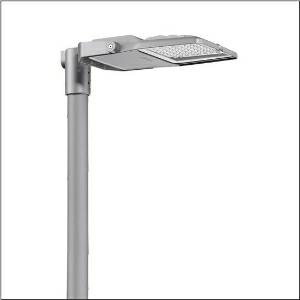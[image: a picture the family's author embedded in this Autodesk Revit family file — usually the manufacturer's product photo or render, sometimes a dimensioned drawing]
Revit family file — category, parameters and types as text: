
# Revit family: floodlight_fl_21_mini___pl43_5xa7775d2a3a_0001
name_source: partatom
category: Lighting Fixtures
units: mm (PartAtom-declared; Revit-internal decimal feet)

## family parameters
Cut with Voids When Loaded = No
Host = Face
Light Source = No
Part Type = Normal
Room Calculation Point = No
Round Connector Dimension = Use Diameter
Shared = No

## types (1)
- --- (1 x LED, 18300 lm, 142.9 W, 3000K)
    Apparent Load = 143 VA
    CIE Flux Codes = 27 78 99 100 100
    Color Rendering = 70
    Color Temperature = 3000K
    Default Elevation = 1800 mm
    Description = Floodlight FL 21 mini, floodlight, primary light control with lens, of PMMA, primary optical cover: protective disc, of toughened safety glass, transparent, light distribution: PL43, light emission: direct distribution, installation type: surface-mounted, LED, High Power LED, rated luminous flux: 18.300lm, luminous efficacy: 128lm/W, light colour: 730, colour temperature: 3000K, control gear: Smart Interface (Zhaga), control: flexible luminous flux parameterisation, time-dependent luminous flux control, constant luminous flux control, overheat protection, pre-setting: logarithmic dimming characteristic, with terminal, 6-pole, mains connection: 220..240V, AC, 50/60Hz, start of lifetime: 143W, end of service life: 151W, reduction: 63W, luminaire housing, of diecast aluminium, powder-coated, Siteco® metallic grey (DB 702S), corrosivity category C5 mid according to DIN EN ISO 12944, suitable for swimming pools, chlorine-resistant, sealing non-destructively replaceable, please order mast flange separately, mast bracket, of steel, galvanised, powder-coated, Siteco® metallic grey (DB 702S), Smart Interface above, protection rating (complete): IP66, insulation class (complete): insulation class II (safety insulation), certification: CE, ENEC, VDE, protection symbol: D, impact resistance: IK08, permissible operating ambient temperature: -40..+40°C, permissible operating ambient temperature for outdoor applications: -40..+50°C, standard: DIN EN 12944, LABS conformity tested according to VDMA 24364:2018-05, packaging unit: 1 piece

Light Distribution: PL43
    Height = 70 mm
    Lamp = 1 x LED
    Lamp Light Flux = 18300 lm
    Lamp Power = 142.9 W
    Lamp count = 1
    Length = 485 mm
    Luminous efficacy = 128 lm/W
    Manufacturer = Siteco
    ModVariant = No
    Model = 5XA7775D2A3A
    Number of Poles = 1
    OnlyDefault = Yes
    Power Factor = 1
    Product Name = Floodlight FL 21 mini | PL43
    Product group = floodlight | pylon annexe
    ProductGroupID = 6200
    Protection Class = Protection class II
    Protection Degree = IP 66
    RLX_Detail_Level = 1
    RLX_Emergency_Light_Flux = 0 lm
    RLX_Emergency_Type = 0
    RLX_Emergency_Type_DB = No
    RlxData = <blob elided: 101321 chars, md5=4b30785b>
    Socket = socket
    Standby Power = 0 W
    System Light Flux = 18300 lm
    System Power = 143 W
    Type Comments = factory setting: luminous flux: 100 % | dim-lin: 254 | 730 mA
    Type Image = l_1007125.jpg
    URL = http://relux.com
    VarID = @adj_160988
    Voltage = 0 V
    Weight = 0.00 kg
    Width = 337 mm

## geometry (parser evidence)
native form markers: Blend x4, Sweep x12
no freeform markers — native parametric forms only
